# Revit family: EKF_EE_ПанелиВертикальныеДляСекционирования(2шт)Trivia_AVERES
name_source: partatom
category: Электрооборудование
units: mm (PartAtom-declared; Revit-internal decimal feet)

## family parameters
Всегда вертикально = Нет
На основе рабочей плоскости = Да
Общий = Да
При загрузке вырезать с полостями = Нет
Размер круглого соединителя = Использовать диаметр
Тип детали = Силовой щит
Точка расчета площади = Нет

## types (6) — shared parameters
ADSK_Единица измерения = шт.
ADSK_Завод-изготовитель = EKF
ADSK_Количество = 1
ADSK_Материал = RAL 7035_Сталь
ADSK_Размер_Глубина = 10 мм
Изготовитель = EKF
Отметка по умолчанию = 1219.2 мм
Серия номенклатуры = Averes
Степень защиты IP = -
ТВ = EKF_2_TRIVIA_AVERES
Тип установки = -
Тип_Панели = Вл_Панели вертикальные для секционирования_2
zero-valued in all types: ADSK_Масса

## per-type parameters (varying)
| type | ADSK_Код изделия | ADSK_Марка | ADSK_Наименование | ADSK_Обозначение | ADSK_Размер_Высота | ADSK_Размер_Ширина | Тип |
| Панели вертикальные для секционирования В1900 Г800 мм (2шт) EKF AVERES | PCV198 | Панели вертикальные для секционирования В1900 Г800 мм (2 шт) EKF AVERES | Панели вертикальные для секционирования В1900 Г800 мм (2 шт) EKF AVERES | Панели вертикальные для секционирования В1900 Г800 мм (2 шт) EKF AVERES | 1900 мм | 716 мм | 719 мм |
| Панели вертикальные для секционирования В1900 Г600 мм (2шт) EKF AVERES | PCV196 | Панели вертикальные для секционирования В1900 Г600 мм (2 шт) EKF AVERES | Панели вертикальные для секционирования В1900 Г600 мм (2 шт) EKF AVERES | Панели вертикальные для секционирования В1900 Г600 мм (2 шт) EKF AVERES | 1900 мм | 516 мм | 718 мм |
| Панели вертикальные для секционирования В1900 Г400 мм (2шт) EKF AVERES | PCV194 | Панели вертикальные для секционирования В1900 Г400 мм (2 шт) EKF AVERES | Панели вертикальные для секционирования В1900 Г400 мм (2 шт) EKF AVERES | Панели вертикальные для секционирования В1900 Г400 мм (2 шт) EKF AVERES | 1900 мм | 316 мм | 717 мм |
| Панели вертикальные для секционирования В1700 Г800 мм (2шт) EKF AVERES | PCV178 | Панели вертикальные для секционирования В1700 Г800 мм (2 шт) EKF AVERES | Панели вертикальные для секционирования В1700 Г800 мм (2 шт) EKF AVERES | Панели вертикальные для секционирования В1700 Г800 мм (2 шт) EKF AVERES | 1700 мм | 716 мм | 715 мм |
| Панели вертикальные для секционирования В1700 Г600 мм (2шт) EKF AVERES | PCV176 | Панели вертикальные для секционирования В1700 Г600 мм (2 шт) EKF AVERES | Панели вертикальные для секционирования В1700 Г600 мм (2 шт) EKF AVERES | Панели вертикальные для секционирования В1700 Г600 мм (2 шт) EKF AVERES | 1700 мм | 516 мм | 714 мм |
| Панели вертикальные для секционирования В1700 Г400 мм (2шт) EKF AVERES | PCV174 | Панели вертикальные для секционирования В1700 Г400 мм (2 шт) EKF AVERES | Панели вертикальные для секционирования В1700 Г400 мм (2 шт) EKF AVERES | Панели вертикальные для секционирования В1700 Г400 мм (2 шт) EKF AVERES | 1700 мм | 316 мм | 713 мм |
